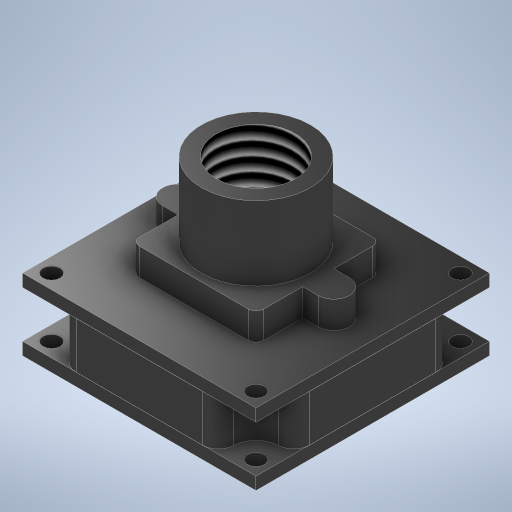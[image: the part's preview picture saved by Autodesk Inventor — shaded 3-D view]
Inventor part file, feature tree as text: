
AUTODESK INVENTOR PART (.ipt)
format: ipt  version: 2024.2 (Build 282272000, 272)  size: 397,824 bytes
history: native  units: mm
features: extrude x5, sketch x2, other x1, hole x1
ambient origin geometry x8: Origin, YZ Plane, XZ Plane, XY Plane, X Axis, Y Axis, Z Axis, Center Point
bodies: Body1 (feature_tree)
feature tree (9):
  other  "ソリッド1"
  sketch  "スケッチ1"
  extrude  "押し出し1"  Depth=30.0mm
  extrude  "押し出し2"  Depth=10.0mm
  extrude  "押し出し3"  Depth=10.0mm
  extrude  "押し出し4"  Depth=10.0mm
  extrude  "押し出し5"  Depth=16.0mm
  hole  "Hole1"  [1 undecoded]
  sketch  "Sketch3"  dims[d0=30.0mm d1=30.0mm d2=26.28mm d3=26.28mm d4=14.0mm d5=16.0mm d6=16.0mm d7=1.0mm d8=20.0mm d9=2.0mm d10=2.2mm d11=4.0mm d12=2.0mm d13=3.0mm d14=0.01mm d15=0.01mm d16=9.2mm d17=0.0mm d18=7.6mm d19=0.0mm d20=1.6mm d21=0.0mm d22=12.7mm d23=0.0mm d24=22.2mm d25=0.0mm d27=10.106mm d28=24.0mm d29=6.1mm d30=3.5mm d31=90.0deg d32=10.0mm d33=0.0mm d34=0.0mm]
note: 1 required parameter value undecoded (feature->parameter linkage not recoverable at this tier; creation-order binding heuristic only, values carry confidence <= 0.55)
